# Revit family: Denver
name_source: partatom
category: Lighting Fixtures
units: mm (PartAtom-declared; Revit-internal decimal feet)

## family parameters
Always vertical = Yes
Cut with Voids When Loaded = No
Host = Ceiling
Light Source = No
OmniClass Number = 23.80.70.11
OmniClass Title = Luminaries for Internal Lighting
Part Type = Normal
Room Calculation Point = No
Round Connector Dimension = Use Diameter
Shared = No

## types (2) — shared parameters
Manufacturer URL - Europe and Rest of World = www.astrolighting.com
Manufacturer URL - North America = us.astrolighting.com
zero-valued in all types: Default Elevation

## per-type parameters (varying)
| type | ADA compliant | Dimmable | Dimming Method | Driver Included | Driver Required | Efficacy (lm/w) | Electrical Class | Lamp | Length of supplied cable | Light Source Fixed | Location / IP Rating | Main Finish | Main Material | Max Drop (pendants) | Power (Watts) | Product CCT | Product CRI | Product Dimensions (MM) | Product Location | Product Name | Product SKU | Product Weight (KG) |
| CE | Not Applicable | Yes | Lamp dependent | Not Applicable | Not Applicable | Lamp dependent | II | 40W max G9 | Not Applicable | Replaceable | IP44 | Polished Chrome | Metal | Not Applicable | Lamp dependent | Lamp dependent | Lamp dependent | See datasheet | Bathroom | Denver | 1038001 | 1 mm  [stored 0.00328084 ft] |
| ETL |  |  |  |  |  |  |  |  |  |  |  |  |  |  |  | 2700K / 3000K | 80/ 90 |  |  |  | 1234567 | 0 mm  [stored 0 ft] |

note: [stored X ft] marks values corroborated as IEEE doubles in the binary element streams (Revit-internal decimal feet)

## geometry (parser evidence)
native form markers: Sweep x3
no freeform markers — native parametric forms only
